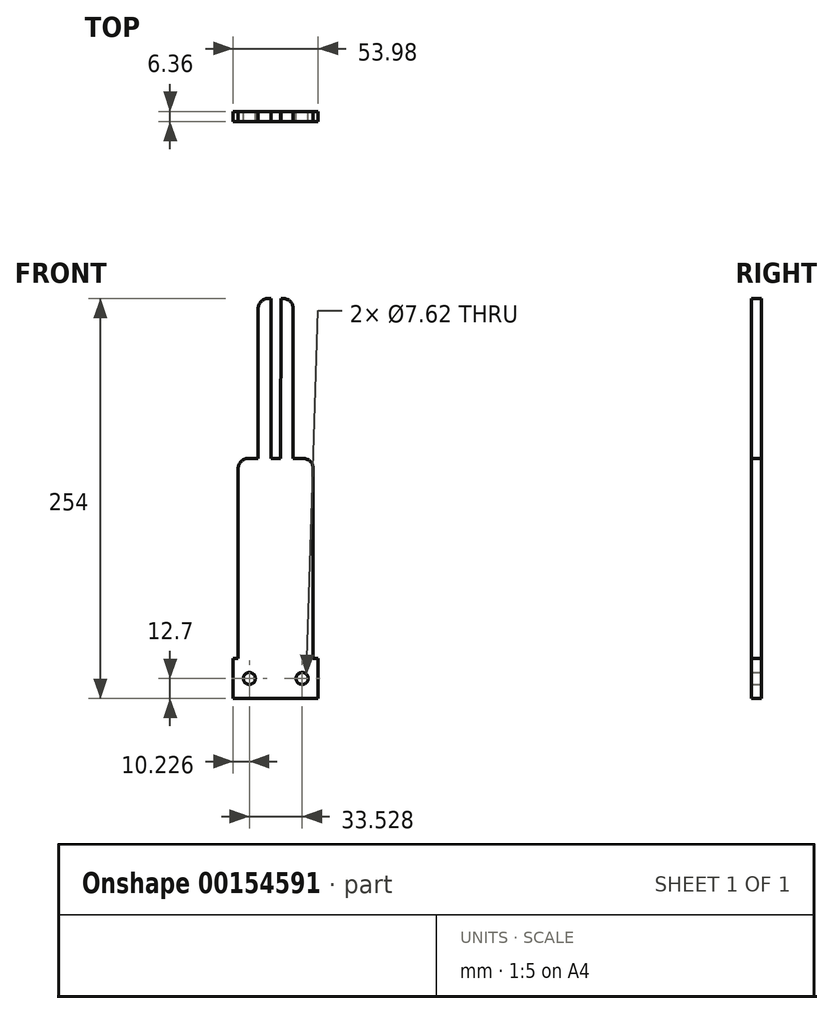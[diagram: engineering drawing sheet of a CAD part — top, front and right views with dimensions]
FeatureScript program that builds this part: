
annotation { "Feature Type Name" : "Feature", "Feature Type Description" : "" }
export const myFeature = defineFeature(function(context is Context, id is Id, definition is map)
    precondition{}
    {
        {
            var Q0;
            Q0=qCreatedBy(makeId("Front.planeOp"),FACE);
            var sketch = newSketch(context, id + "F0", { "sketchPlane" : qUnion([Q0])});
            skLineSegment(sketch, "E0.bottom", {"start": v(26.99, 12.7) * mm, "end": v(23.81, 12.7) * mm});
            skLineSegment(sketch, "E0.top", {"start": v(26.99, -12.7) * mm, "end": v(-26.99, -12.7) * mm});
            skLineSegment(sketch, "E0.left", {"start": v(26.99, 12.7) * mm, "end": v(26.99, -12.7) * mm});
            skLineSegment(sketch, "E0.right", {"start": v(-26.99, 12.7) * mm, "end": v(-26.99, -12.7) * mm});
            skPoint(sketch, "E0.middle", {"position": v(0, 0) * mm});
            skLineSegment(sketch, "E1", {"start": v(0, 0) * mm, "end": v(0, -12.7) * mm});
            skLineSegment(sketch, "E2", {"start": v(-23.81, 12.7) * mm, "end": v(-23.81, 133.35) * mm});
            skLineSegment(sketch, "E3", {"start": v(-17.46, 139.7) * mm, "end": v(-11.11, 139.7) * mm});
            skLineSegment(sketch, "E4", {"start": v(23.81, 133.35) * mm, "end": v(23.81, 12.7) * mm});
            skLineSegment(sketch, "E5", {"start": v(-4.76, 241.3) * mm, "end": v(-3.14, 241.3) * mm});
            skLineSegment(sketch, "E6", {"start": v(11.11, 234.95) * mm, "end": v(11.11, 139.7) * mm});
            skLineSegment(sketch, "E7.trimOffspring", {"start": v(-11.11, 139.7) * mm, "end": v(-11.11, 234.95) * mm});
            skLineSegment(sketch, "E8.trimOffspring", {"start": v(-3.14, 139.7) * mm, "end": v(3.17, 139.7) * mm});
            skLineSegment(sketch, "E9.trimOffspring", {"start": v(11.11, 139.7) * mm, "end": v(17.46, 139.7) * mm});
            skLineSegment(sketch, "E10.trimOffspring", {"start": v(-23.81, 12.7) * mm, "end": v(-26.99, 12.7) * mm});
            skLineSegment(sketch, "E11", {"start": v(-3.14, 139.7) * mm, "end": v(-3.14, 241.3) * mm});
            skLineSegment(sketch, "E12", {"start": v(3.2, 241.3) * mm, "end": v(3.17, 139.7) * mm});
            skLineSegment(sketch, "E13.trimOffspring", {"start": v(3.2, 241.3) * mm, "end": v(4.76, 241.3) * mm});
            skPoint(sketch, "E14.visualSharp", {"position": v(-11.11, 241.3) * mm});
            skArc(sketch, "E14.filletArc", {"start": v(-4.76, 241.3) * mm, "mid": v(-9.25, 239.44) * mm, "end": v(-11.11, 234.95) * mm});
            skPoint(sketch, "E15.visualSharp", {"position": v(11.11, 241.3) * mm});
            skArc(sketch, "E15.filletArc", {"start": v(11.11, 234.95) * mm, "mid": v(9.25, 239.44) * mm, "end": v(4.76, 241.3) * mm});
            skPoint(sketch, "E16.visualSharp", {"position": v(23.81, 139.7) * mm});
            skArc(sketch, "E16.filletArc", {"start": v(23.81, 133.35) * mm, "mid": v(21.95, 137.84) * mm, "end": v(17.46, 139.7) * mm});
            skPoint(sketch, "E17.visualSharp", {"position": v(-23.81, 139.7) * mm});
            skArc(sketch, "E17.filletArc", {"start": v(-17.46, 139.7) * mm, "mid": v(-21.95, 137.84) * mm, "end": v(-23.81, 133.35) * mm});
            skCircle(sketch, "E18", {"center": v(-16.76, 0) * mm, "radius": 3.81 * mm});
            skCircle(sketch, "E19", {"center": v(16.76, 0) * mm, "radius": 3.81 * mm});
            skLineSegment(sketch, "E20", {"start": v(0, -12.7) * mm, "end": v(-3.17, -12.7) * mm});
            skLineSegment(sketch, "E21", {"start": v(-3.17, -12.7) * mm, "end": v(-3.17, 14.57) * mm, "construction": true});
            skLineSegment(sketch, "E22.MirrorCS", {"start": v(3.17, -12.7) * mm, "end": v(3.17, 14.57) * mm, "construction": true});
            skSolve(sketch);
        }
        {
            var Q0;
            Q0 = qSketchRegion(id + "F0", true);
            extrude(context, id + "F1", {"entities" : qUnion([Q0]), "endBound" : BoundingType.SYMMETRIC, "depth" : 6.35 * mm});
        }
    });
